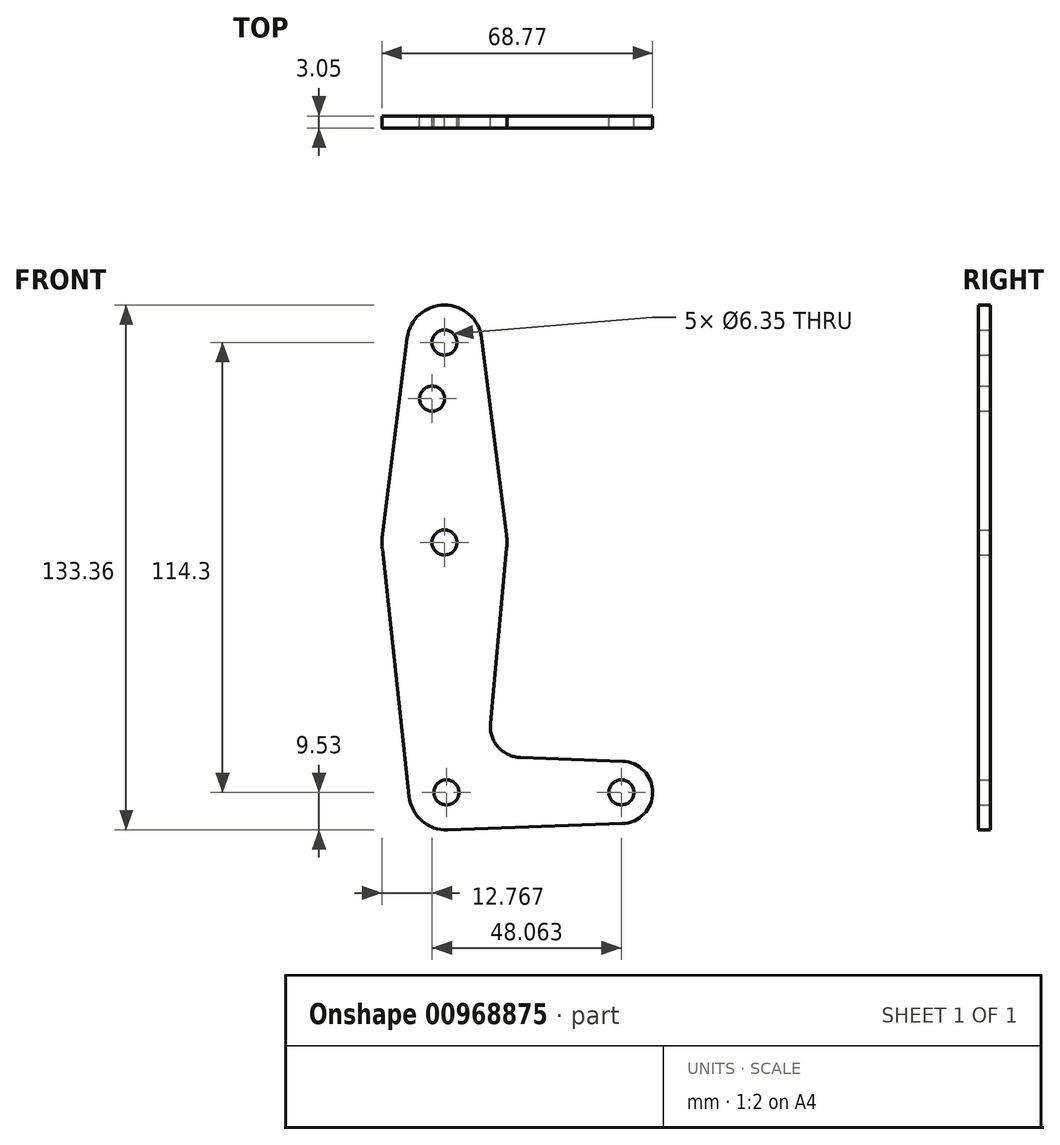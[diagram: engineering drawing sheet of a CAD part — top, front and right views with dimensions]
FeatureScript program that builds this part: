
annotation { "Feature Type Name" : "Feature", "Feature Type Description" : "" }
export const myFeature = defineFeature(function(context is Context, id is Id, definition is map)
    precondition{}
    {
        {
            var Q0;
            Q0=qCreatedBy(makeId("Front.planeOp"),FACE);
            var sketch = newSketch(context, id + "F0", { "sketchPlane" : qUnion([Q0])});
            skLineSegment(sketch, "E0", {"start": v(0, 0) * mm, "end": v(44.45, 0) * mm, "construction": true});
            skCircle(sketch, "E1", {"center": v(-0.5, 63.5) * mm, "radius": 15.88 * mm});
            skCircle(sketch, "E2", {"center": v(-0.5, 114.3) * mm, "radius": 9.53 * mm});
            skCircle(sketch, "E3", {"center": v(0, 0) * mm, "radius": 9.53 * mm});
            skCircle(sketch, "E4", {"center": v(44.45, 0) * mm, "radius": 7.94 * mm});
            skLineSegment(sketch, "E5", {"start": v(8.95, 115.5) * mm, "end": v(15.48, 63.64) * mm});
            skLineSegment(sketch, "E6", {"start": v(-9.95, 115.5) * mm, "end": v(-16.48, 63.64) * mm});
            skLineSegment(sketch, "E7", {"start": v(0, -9.53) * mm, "end": v(44.73, -7.93) * mm});
            skCircle(sketch, "E8", {"center": v(-0.5, 114.3) * mm, "radius": 3.18 * mm});
            skCircle(sketch, "E9", {"center": v(-3.61, 100.03) * mm, "radius": 3.18 * mm});
            skCircle(sketch, "E10", {"center": v(-0.5, 63.5) * mm, "radius": 3.18 * mm});
            skCircle(sketch, "E11", {"center": v(0, 0) * mm, "radius": 3.18 * mm});
            skCircle(sketch, "E12", {"center": v(44.45, 0) * mm, "radius": 3.18 * mm});
            skLineSegment(sketch, "E13", {"start": v(15.46, 63.7) * mm, "end": v(11.19, 17.54) * mm});
            skLineSegment(sketch, "E14", {"start": v(18.82, 8.86) * mm, "end": v(44.73, 7.93) * mm});
            skLineSegment(sketch, "E15", {"start": v(-16.48, 63.64) * mm, "end": v(-9.47, -1.03) * mm});
            skArc(sketch, "E16.filletArc", {"start": v(11.19, 17.54) * mm, "mid": v(13.14, 11.55) * mm, "end": v(18.82, 8.86) * mm});
            skLineSegment(sketch, "E17", {"start": v(-0.5, 114.3) * mm, "end": v(0, 0) * mm});
            skSolve(sketch);
        }
        {
            var Q0;
            {var subQ4=sQuery(id+"F0.wireOp",EDGE,"E1");var subQ6=sQuery(id+"F0.wireOp",EDGE,"E6");var subQ9=makeQuery(id+"F0.imprint","INTERSECT",VERTEX,{"derivedFrom":[subQ4,subQ6]});Q0=makeQuery(id+"F0.imprint","IMPRINT",FACE,{"disambiguationData":[TD([[makeQuery(id+"F0.imprint","IMPRINT",EDGE,{"disambiguationData":[TD([[subQ9,1.0]])],"derivedFrom":subQ4}),-1.0]])]});}
            var Q1;
            Q1=makeQuery(id+"F0.imprint","IMPRINT",FACE,{"disambiguationData":[TD([[makeQuery(id+"F0.imprint","IMPRINT",EDGE,{"derivedFrom":sQuery(id+"F0.wireOp",EDGE,"E8")}),-1.0]])]});
            var Q2;
            {var subQ4=sQuery(id+"F0.wireOp",EDGE,"E5");var subQ8=sQuery(id+"F0.wireOp",EDGE,"E1");var subQ9=makeQuery(id+"F0.imprint","INTERSECT",VERTEX,{"derivedFrom":[subQ8,subQ4]});Q2=makeQuery(id+"F0.imprint","IMPRINT",FACE,{"disambiguationData":[TD([[makeQuery(id+"F0.imprint","IMPRINT",EDGE,{"disambiguationData":[TD([[subQ9,-1.0]])],"derivedFrom":subQ8}),-1.0]])]});}
            var Q3;
            {var subQ4=sQuery(id+"F0.wireOp",EDGE,"E1");var subQ5=makeQuery(id+"F0.imprint","INTERSECT",VERTEX,{"derivedFrom":[subQ4,sQuery(id+"F0.wireOp",EDGE,"E5")]});Q3=makeQuery(id+"F0.imprint","IMPRINT",FACE,{"disambiguationData":[TD([[makeQuery(id+"F0.imprint","IMPRINT",EDGE,{"disambiguationData":[TD([[subQ5,-1.0]])],"derivedFrom":subQ4}),1.0]])]});}
            var Q4;
            {var subQ0=sQuery(id+"F0.wireOp",EDGE,"E1");var subQ4=makeQuery(id+"F0.imprint","INTERSECT",VERTEX,{"derivedFrom":[subQ0,sQuery(id+"F0.wireOp",EDGE,"E6")]});Q4=makeQuery(id+"F0.imprint","IMPRINT",FACE,{"disambiguationData":[TD([[makeQuery(id+"F0.imprint","IMPRINT",EDGE,{"disambiguationData":[TD([[subQ4,1.0]])],"derivedFrom":subQ0}),1.0]])]});}
            var Q5;
            {var subQ0=sQuery(id+"F0.wireOp",EDGE,"E15");var subQ1=sQuery(id+"F0.wireOp",EDGE,"E1");var subQ2=makeQuery(id+"F0.imprint","INTERSECT",VERTEX,{"derivedFrom":[subQ1,subQ0]});Q5=makeQuery(id+"F0.imprint","IMPRINT",FACE,{"disambiguationData":[TD([[makeQuery(id+"F0.imprint","IMPRINT",EDGE,{"disambiguationData":[TD([[subQ2,-1.0]])],"derivedFrom":subQ1}),-1.0]])]});}
            var Q6;
            {var subQ5=sQuery(id+"F0.wireOp",EDGE,"E14");Q6=makeQuery(id+"F0.imprint","IMPRINT",FACE,{"disambiguationData":[TD([[makeQuery(id+"F0.imprint","IMPRINT",EDGE,{"derivedFrom":subQ5}),-1.0]])]});}
            var Q7;
            Q7=makeQuery(id+"F0.imprint","IMPRINT",FACE,{"disambiguationData":[TD([[makeQuery(id+"F0.imprint","IMPRINT",EDGE,{"derivedFrom":sQuery(id+"F0.wireOp",EDGE,"E11")}),-1.0]])]});
            var Q8;
            Q8=makeQuery(id+"F0.imprint","IMPRINT",FACE,{"disambiguationData":[TD([[makeQuery(id+"F0.imprint","IMPRINT",EDGE,{"derivedFrom":sQuery(id+"F0.wireOp",EDGE,"E12")}),-1.0]])]});
            extrude(context, id + "F1", {"entities" : qUnion([Q0, Q1, Q2, Q3, Q4, Q5, Q6, Q7, Q8]), "depth" : 3.05 * mm, "offsetDistance" : 25.4 * mm});
        }
    });
